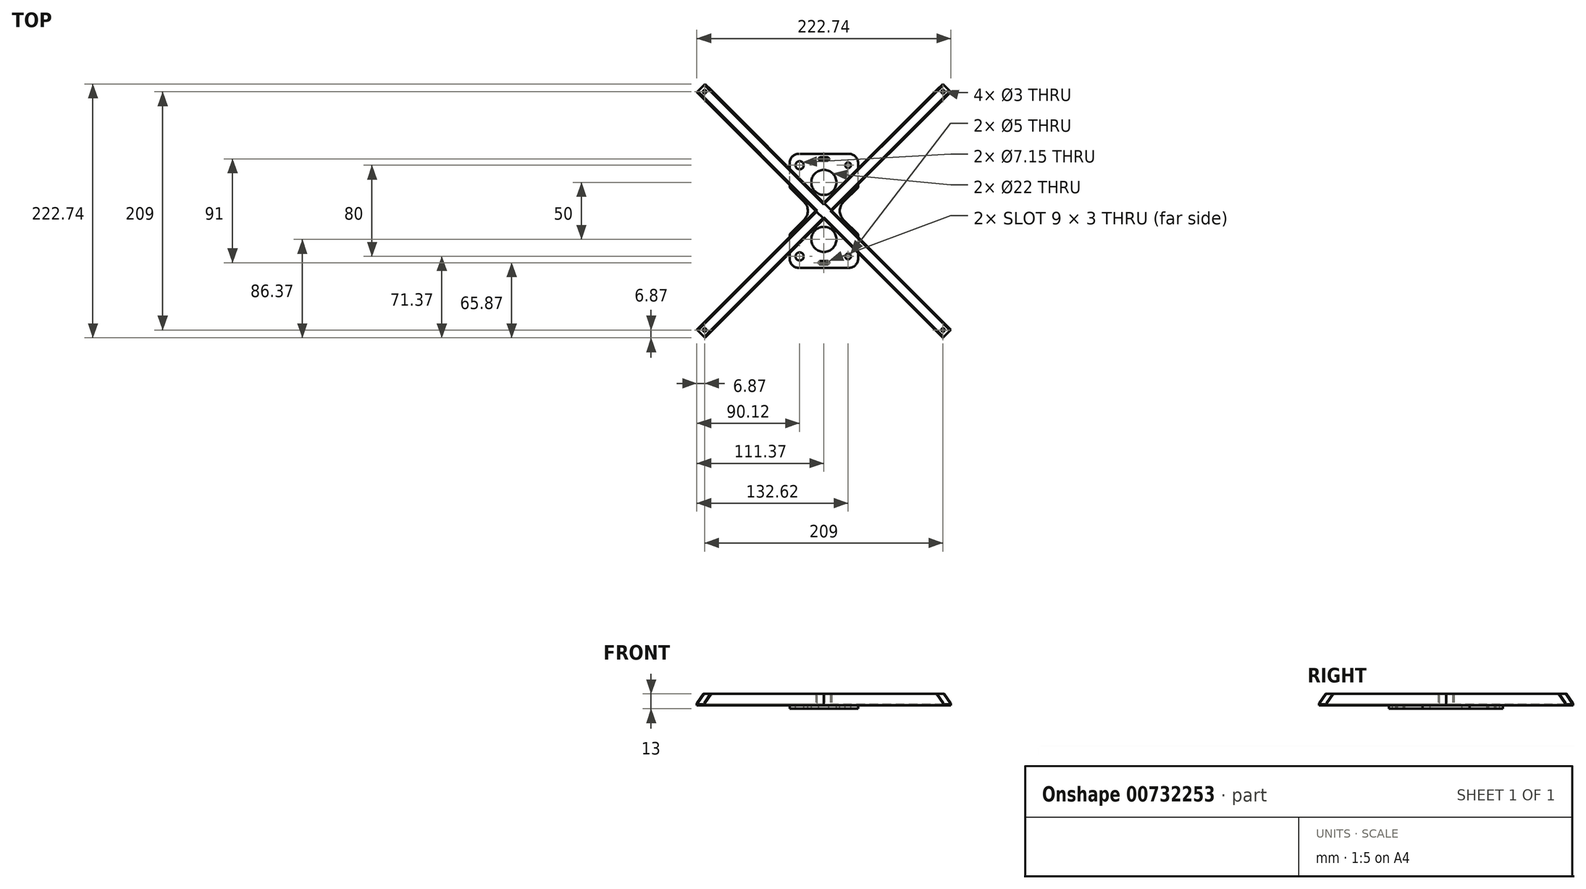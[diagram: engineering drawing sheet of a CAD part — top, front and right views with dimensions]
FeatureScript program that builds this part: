
annotation { "Feature Type Name" : "Feature", "Feature Type Description" : "" }
export const myFeature = defineFeature(function(context is Context, id is Id, definition is map)
    precondition{}
    {
        {
            var Q0;
            Q0=qCreatedBy(makeId("Top.planeOp"),FACE);
            var sketch = newSketch(context, id + "F0", { "sketchPlane" : qUnion([Q0])});
            skLineSegment(sketch, "E0.bottom", {"start": v(30, -50) * mm, "end": v(-30, -50) * mm});
            skLineSegment(sketch, "E0.top", {"start": v(30, 50) * mm, "end": v(-30, 50) * mm});
            skLineSegment(sketch, "E0.left", {"start": v(30, -50) * mm, "end": v(30, 50) * mm});
            skLineSegment(sketch, "E0.right", {"start": v(-30, -50) * mm, "end": v(-30, 50) * mm});
            skPoint(sketch, "E0.middle", {"position": v(0, 0) * mm});
            skSolve(sketch);
        }
        {
            var Q0;
            Q0=qSketchRegion(id+"F0",true);
            extrude(context, id + "F1", {"entities" : qUnion([Q0]), "depth" : 3 * mm, "offsetDistance" : 25 * mm});
        }
        {
            var Q0;
            Q0=makeQuery(id+"F1.opExtrude","CAP_FACE",FACE,{"disambiguationData":[OSD([sQuery(id+"F0.wireOp",EDGE,"E0.bottom"),sQuery(id+"F0.wireOp",EDGE,"E0.top"),sQuery(id+"F0.wireOp",EDGE,"E0.left"),sQuery(id+"F0.wireOp",EDGE,"E0.right")])],"isStart":false});
            var sketch = newSketch(context, id + "F2", { "sketchPlane" : qUnion([Q0])});
            skCircle(sketch, "E1", {"center": v(0, 25) * mm, "radius": 11 * mm});
            skCircle(sketch, "E2", {"center": v(0, -25) * mm, "radius": 11 * mm});
            skCircle(sketch, "E3", {"center": v(25, 0) * mm, "radius": 11 * mm});
            skCircle(sketch, "E4", {"center": v(-25, 0) * mm, "radius": 11 * mm});
            skLineSegment(sketch, "E5", {"start": v(-3, 45.5) * mm, "end": v(3, 45.5) * mm});
            skLineSegment(sketch, "E6", {"start": v(-3, -45.5) * mm, "end": v(3, -45.5) * mm});
            skPoint(sketch, "E7", {"position": v(0, 45.5) * mm});
            skArc(sketch, "E8.0.startCap", {"start": v(-3, 44) * mm, "mid": v(-4.5, 45.5) * mm, "end": v(-3, 47) * mm});
            skArc(sketch, "E8.0.endCap", {"start": v(3, 47) * mm, "mid": v(4.5, 45.5) * mm, "end": v(3, 44) * mm});
            skLineSegment(sketch, "E8.0.left", {"start": v(-3, 47) * mm, "end": v(3, 47) * mm});
            skLineSegment(sketch, "E8.0.right", {"start": v(-3, 44) * mm, "end": v(3, 44) * mm});
            skArc(sketch, "E9.0.startCap", {"start": v(-3, -47) * mm, "mid": v(-4.5, -45.5) * mm, "end": v(-3, -44) * mm});
            skArc(sketch, "E9.0.endCap", {"start": v(3, -44) * mm, "mid": v(4.5, -45.5) * mm, "end": v(3, -47) * mm});
            skLineSegment(sketch, "E9.0.left", {"start": v(-3, -44) * mm, "end": v(3, -44) * mm});
            skLineSegment(sketch, "E9.0.right", {"start": v(-3, -47) * mm, "end": v(3, -47) * mm});
            skSolve(sketch);
        }
        {
            var Q0;
            Q0=makeQuery(id+"F2.imprint","IMPRINT",FACE,{"disambiguationData":[TD([[makeQuery(id+"F2.imprint","IMPRINT",EDGE,{"derivedFrom":sQuery(id+"F2.wireOp",EDGE,"E1")}),-1.0]])]});
            var sketch = newSketch(context, id + "F3", { "sketchPlane" : qUnion([Q0])});
            skLineSegment(sketch, "E10.bottom", {"start": v(21.25, 40) * mm, "end": v(-21.25, 40) * mm, "construction": true});
            skLineSegment(sketch, "E10.top", {"start": v(21.25, -40) * mm, "end": v(-21.25, -40) * mm, "construction": true});
            skLineSegment(sketch, "E10.left", {"start": v(21.25, 40) * mm, "end": v(21.25, -40) * mm, "construction": true});
            skLineSegment(sketch, "E10.right", {"start": v(-21.25, 40) * mm, "end": v(-21.25, -40) * mm, "construction": true});
            skPoint(sketch, "E10.middle", {"position": v(0, 0) * mm});
            skCircle(sketch, "E11", {"center": v(21.25, 40) * mm, "radius": 2.5 * mm});
            skCircle(sketch, "E12", {"center": v(21.25, -40) * mm, "radius": 2.5 * mm});
            skCircle(sketch, "E13", {"center": v(-21.25, -40) * mm, "radius": 3.58 * mm});
            skCircle(sketch, "E14", {"center": v(-21.25, 40) * mm, "radius": 3.57 * mm});
            skSolve(sketch);
        }
        {
            var Q0;
            Q0=qSketchRegion(id+"F3",true);
            extrude(context, id + "F4", {"entities" : qUnion([Q0]), "operationType" : NewBodyOperationType.REMOVE, "endBound" : BoundingType.THROUGH_ALL, "oppositeDirection" : true, "depth" : 25 * mm, "offsetDistance" : 25 * mm});
        }
        {
            var Q0;
            Q0=qSketchRegion(id+"F2",true);
            extrude(context, id + "F5", {"entities" : qUnion([Q0]), "operationType" : NewBodyOperationType.REMOVE, "endBound" : BoundingType.THROUGH_ALL, "oppositeDirection" : true, "depth" : 25 * mm, "offsetDistance" : 25 * mm});
        }
        {
            var Q0;
            Q0=makeQuery(id+"F1.opExtrude","CAP_FACE",FACE,{"disambiguationData":[OSD([sQuery(id+"F0.wireOp",EDGE,"E0.bottom"),sQuery(id+"F0.wireOp",EDGE,"E0.top"),sQuery(id+"F0.wireOp",EDGE,"E0.left"),sQuery(id+"F0.wireOp",EDGE,"E0.right")])],"isStart":false});
            var sketch = newSketch(context, id + "F6", { "sketchPlane" : qUnion([Q0])});
            skLineSegment(sketch, "E15", {"start": v(30, 20.56) * mm, "end": v(30, -20.56) * mm});
            skLineSegment(sketch, "E16", {"start": v(30, -20.56) * mm, "end": v(17.22, -7.78) * mm});
            skLineSegment(sketch, "E17", {"start": v(17.22, -7.78) * mm, "end": v(17.22, 7.78) * mm});
            skLineSegment(sketch, "E18", {"start": v(17.22, 7.78) * mm, "end": v(30, 20.56) * mm});
            skLineSegment(sketch, "E19", {"start": v(-30, 20.56) * mm, "end": v(-17.22, 7.78) * mm});
            skLineSegment(sketch, "E20", {"start": v(-17.22, 7.78) * mm, "end": v(-17.22, -7.78) * mm});
            skLineSegment(sketch, "E21", {"start": v(-17.22, -7.78) * mm, "end": v(-30, -20.56) * mm});
            skLineSegment(sketch, "E22", {"start": v(-30, -20.56) * mm, "end": v(-30, 20.56) * mm});
            skSolve(sketch);
        }
        {
            var Q0;
            Q0=qSketchRegion(id+"F6",true);
            extrude(context, id + "F7", {"entities" : qUnion([Q0]), "operationType" : NewBodyOperationType.REMOVE, "endBound" : BoundingType.THROUGH_ALL, "oppositeDirection" : true, "depth" : 25 * mm, "offsetDistance" : 25 * mm});
        }
        {
            var Q0;
            Q0=makeQuery(id+"F1.opExtrude","SWEPT_EDGE",EDGE,{"disambiguationData":[OSD([sQuery(id+"F0.wireOp",EDGE,"E0.bottom"),sQuery(id+"F0.wireOp",EDGE,"E0.left")])]});
            var Q1;
            Q1=makeQuery(id+"F1.opExtrude","SWEPT_EDGE",EDGE,{"disambiguationData":[OSD([sQuery(id+"F0.wireOp",EDGE,"E0.bottom"),sQuery(id+"F0.wireOp",EDGE,"E0.right")])]});
            var Q2;
            Q2=makeQuery(id+"F1.opExtrude","SWEPT_EDGE",EDGE,{"disambiguationData":[OSD([sQuery(id+"F0.wireOp",EDGE,"E0.top"),sQuery(id+"F0.wireOp",EDGE,"E0.left")])]});
            var Q3;
            Q3=makeQuery(id+"F1.opExtrude","SWEPT_EDGE",EDGE,{"disambiguationData":[OSD([sQuery(id+"F0.wireOp",EDGE,"E0.top"),sQuery(id+"F0.wireOp",EDGE,"E0.right")])]});
            fillet(context, id + "F8", {"entities" : qUnion([Q0, Q1, Q2, Q3]), "radius" : 8 * mm, "tangentPropagation" : true, "allowEdgeOverflow" : false});
        }
        {
            var Q0;
            Q0=makeQuery(id+"F1.opExtrude","CAP_FACE",FACE,{"disambiguationData":[OSD([sQuery(id+"F0.wireOp",EDGE,"E0.bottom"),sQuery(id+"F0.wireOp",EDGE,"E0.top"),sQuery(id+"F0.wireOp",EDGE,"E0.left"),sQuery(id+"F0.wireOp",EDGE,"E0.right")])],"isStart":false});
            var sketch = newSketch(context, id + "F9", { "sketchPlane" : qUnion([Q0])});
            skLineSegment(sketch, "E23", {"start": v(-107.83, 107.83) * mm, "end": v(107.83, -107.83) * mm, "construction": true});
            skLineSegment(sketch, "E24", {"start": v(-104.3, 111.37) * mm, "end": v(-111.37, 104.3) * mm});
            skLineSegment(sketch, "E25", {"start": v(-111.37, 104.3) * mm, "end": v(104.3, -111.37) * mm});
            skLineSegment(sketch, "E26", {"start": v(104.3, -111.37) * mm, "end": v(111.37, -104.3) * mm});
            skLineSegment(sketch, "E27", {"start": v(111.37, -104.3) * mm, "end": v(-104.3, 111.37) * mm});
            skSolve(sketch);
        }
        {
            var Q0;
            Q0=qSketchRegion(id+"F9",true);
            extrude(context, id + "F10", {"entities" : qUnion([Q0]), "depth" : 10 * mm, "offsetDistance" : 25 * mm});
        }
        {
            var Q0;
            Q0=makeQuery(id+"F10.opExtrude","CAP_FACE",FACE,{"disambiguationData":[OSD([sQuery(id+"F9.wireOp",EDGE,"E24"),sQuery(id+"F9.wireOp",EDGE,"E25"),sQuery(id+"F9.wireOp",EDGE,"E26"),sQuery(id+"F9.wireOp",EDGE,"E27")])],"isStart":false});
            var sketch = newSketch(context, id + "F11", { "sketchPlane" : qUnion([Q0])});
            skLineSegment(sketch, "E28", {"start": v(-105, 110.66) * mm, "end": v(-110.66, 105) * mm});
            skLineSegment(sketch, "E29", {"start": v(-110.66, 105) * mm, "end": v(105, -110.66) * mm});
            skLineSegment(sketch, "E30", {"start": v(105, -110.66) * mm, "end": v(110.66, -105) * mm});
            skLineSegment(sketch, "E31", {"start": v(110.66, -105) * mm, "end": v(-105, 110.66) * mm});
            skSolve(sketch);
        }
        {
            var Q0;
            Q0=qSketchRegion(id+"F11",true);
            extrude(context, id + "F12", {"entities" : qUnion([Q0]), "operationType" : NewBodyOperationType.REMOVE, "oppositeDirection" : true, "depth" : 9 * mm, "offsetDistance" : 25 * mm});
        }
        {
            var Q0;
            Q0=makeQuery(id+"F10.opExtrude","SWEPT_FACE",FACE,{"disambiguationData":[OSD([sQuery(id+"F9.wireOp",EDGE,"E27")])]});
            var sketch = newSketch(context, id + "F13", { "sketchPlane" : qUnion([Q0])});
            skLineSegment(sketch, "E32.bottom", {"start": v(5, 13) * mm, "end": v(-5, 13) * mm});
            skLineSegment(sketch, "E32.top", {"start": v(5, 3) * mm, "end": v(-5, 3) * mm});
            skLineSegment(sketch, "E32.left", {"start": v(5, 13) * mm, "end": v(5, 3) * mm});
            skLineSegment(sketch, "E32.right", {"start": v(-5, 13) * mm, "end": v(-5, 3) * mm});
            skSolve(sketch);
        }
        {
            var Q0;
            Q0=qSketchRegion(id+"F13",true);
            extrude(context, id + "F14", {"entities" : qUnion([Q0]), "depth" : (305 / 2 - 5) * mm, "offsetDistance" : 25 * mm});
        }
        {
            var Q0;
            Q0=makeQuery(id+"F14.opExtrude","CAP_FACE",FACE,{"disambiguationData":[OSD([sQuery(id+"F13.wireOp",EDGE,"E32.bottom"),sQuery(id+"F13.wireOp",EDGE,"E32.top"),sQuery(id+"F13.wireOp",EDGE,"E32.left"),sQuery(id+"F13.wireOp",EDGE,"E32.right")])],"isStart":false});
            var sketch = newSketch(context, id + "F15", { "sketchPlane" : qUnion([Q0])});
            skLineSegment(sketch, "E33.bottom", {"start": v(4, 13) * mm, "end": v(-4, 13) * mm});
            skLineSegment(sketch, "E33.top", {"start": v(4, 4) * mm, "end": v(-4, 4) * mm});
            skLineSegment(sketch, "E33.left", {"start": v(4, 13) * mm, "end": v(4, 4) * mm});
            skLineSegment(sketch, "E33.right", {"start": v(-4, 13) * mm, "end": v(-4, 4) * mm});
            skSolve(sketch);
        }
        {
            var Q0;
            Q0=qSketchRegion(id+"F15",true);
            extrude(context, id + "F16", {"entities" : qUnion([Q0]), "operationType" : NewBodyOperationType.REMOVE, "endBound" : BoundingType.THROUGH_ALL, "oppositeDirection" : true, "depth" : 25 * mm, "offsetDistance" : 25 * mm});
        }
        {
            var Q0;
            Q0=qCreatedBy(makeId("Front.planeOp"),FACE);
            var Q1;
            Q1=qCreatedBy(makeId("Right.planeOp"),FACE);
            cPlane(context, id + "F17", {"entities" : qUnion([Q0, Q1]), "cplaneType" : CPlaneType.MID_PLANE, "offset" : 25 * mm, "width" : 150 * mm, "height" : 150 * mm});
        }
        {
            var Q0;
            Q0=makeQuery(id+"F14.opExtrude","SWEPT_BODY",BODY,{"disambiguationData":[OSD([sQuery(id+"F13.wireOp",EDGE,"E32.bottom"),sQuery(id+"F13.wireOp",EDGE,"E32.top"),sQuery(id+"F13.wireOp",EDGE,"E32.left"),sQuery(id+"F13.wireOp",EDGE,"E32.right")])]});
            var Q1;
            Q1=qCreatedBy(id+"F17.planeOp",FACE);
            mirror(context, id + "F18", {"entities" : qUnion([Q0]), "mirrorPlane" : qUnion([Q1])});
        }
        {
            var Q0;
            {var subQ0=sQuery(id+"F13.wireOp",EDGE,"E32.bottom");var subQ1=sQuery(id+"F13.wireOp",EDGE,"E32.left");Q0=makeQuery(id+"F16.boolean.opBoolean","SPLIT",EDGE,{"disambiguationData":[TD([makeQuery(id+"F14.opExtrude","SWEPT_FACE",FACE,{"disambiguationData":[OSD([subQ1])]})])],"derivedFrom":makeQuery(id+"F14.opExtrude","CAP_EDGE",EDGE,{"disambiguationData":[OSD([subQ0])],"isStart":false})});}
            var Q1;
            {var subQ0=sQuery(id+"F13.wireOp",EDGE,"E32.bottom");var subQ1=sQuery(id+"F13.wireOp",EDGE,"E32.right");Q1=makeQuery(id+"F16.boolean.opBoolean","SPLIT",EDGE,{"disambiguationData":[TD([makeQuery(id+"F14.opExtrude","SWEPT_FACE",FACE,{"disambiguationData":[OSD([subQ1])]})])],"derivedFrom":makeQuery(id+"F14.opExtrude","CAP_EDGE",EDGE,{"disambiguationData":[OSD([subQ0])],"isStart":false})});}
            var Q2;
            {var subQ0=sQuery(id+"F9.wireOp",EDGE,"E26");var subQ1=sQuery(id+"F9.wireOp",EDGE,"E25");Q2=makeQuery(id+"F12.boolean.opBoolean","SPLIT",EDGE,{"disambiguationData":[TD([makeQuery(id+"F10.opExtrude","SWEPT_FACE",FACE,{"disambiguationData":[OSD([subQ1])]})])],"derivedFrom":makeQuery(id+"F10.opExtrude","CAP_EDGE",EDGE,{"disambiguationData":[OSD([subQ0])],"isStart":false})});}
            var Q3;
            {var subQ0=sQuery(id+"F9.wireOp",EDGE,"E27");var subQ1=sQuery(id+"F9.wireOp",EDGE,"E26");Q3=makeQuery(id+"F12.boolean.opBoolean","SPLIT",EDGE,{"disambiguationData":[TD([makeQuery(id+"F10.opExtrude","SWEPT_FACE",FACE,{"disambiguationData":[OSD([subQ0])]})])],"derivedFrom":makeQuery(id+"F10.opExtrude","CAP_EDGE",EDGE,{"disambiguationData":[OSD([subQ1])],"isStart":false})});}
            var Q4;
            {var subQ0=sQuery(id+"F13.wireOp",EDGE,"E32.bottom");var subQ1=sQuery(id+"F13.wireOp",EDGE,"E32.right");Q4=makeQuery(id+"F18.opPattern","COPY",EDGE,{"derivedFrom":makeQuery(id+"F16.boolean.opBoolean","SPLIT",EDGE,{"disambiguationData":[TD([makeQuery(id+"F14.opExtrude","SWEPT_FACE",FACE,{"disambiguationData":[OSD([subQ1])]})])],"derivedFrom":makeQuery(id+"F14.opExtrude","CAP_EDGE",EDGE,{"disambiguationData":[OSD([subQ0])],"isStart":false})}),"instanceName":"1"});}
            var Q5;
            {var subQ0=sQuery(id+"F13.wireOp",EDGE,"E32.bottom");var subQ1=sQuery(id+"F13.wireOp",EDGE,"E32.left");Q5=makeQuery(id+"F18.opPattern","COPY",EDGE,{"derivedFrom":makeQuery(id+"F16.boolean.opBoolean","SPLIT",EDGE,{"disambiguationData":[TD([makeQuery(id+"F14.opExtrude","SWEPT_FACE",FACE,{"disambiguationData":[OSD([subQ1])]})])],"derivedFrom":makeQuery(id+"F14.opExtrude","CAP_EDGE",EDGE,{"disambiguationData":[OSD([subQ0])],"isStart":false})}),"instanceName":"1"});}
            var Q6;
            {var subQ0=sQuery(id+"F9.wireOp",EDGE,"E24");var subQ1=sQuery(id+"F9.wireOp",EDGE,"E27");Q6=makeQuery(id+"F12.boolean.opBoolean","SPLIT",EDGE,{"disambiguationData":[TD([makeQuery(id+"F10.opExtrude","SWEPT_FACE",FACE,{"disambiguationData":[OSD([subQ1])]})])],"derivedFrom":makeQuery(id+"F10.opExtrude","CAP_EDGE",EDGE,{"disambiguationData":[OSD([subQ0])],"isStart":false})});}
            var Q7;
            {var subQ0=sQuery(id+"F9.wireOp",EDGE,"E24");var subQ1=sQuery(id+"F9.wireOp",EDGE,"E25");Q7=makeQuery(id+"F12.boolean.opBoolean","SPLIT",EDGE,{"disambiguationData":[TD([makeQuery(id+"F10.opExtrude","SWEPT_FACE",FACE,{"disambiguationData":[OSD([subQ1])]})])],"derivedFrom":makeQuery(id+"F10.opExtrude","CAP_EDGE",EDGE,{"disambiguationData":[OSD([subQ0])],"isStart":false})});}
            chamfer(context, id + "F19", {"entities" : qUnion([Q0, Q1, Q2, Q3, Q4, Q5, Q6, Q7]), "width" : 8 * mm, "tangentPropagation" : true});
        }
        {
            var Q0;
            Q0=makeQuery(id+"F12.boolean.opBoolean","COPY",FACE,{"derivedFrom":makeQuery(id+"F12.opExtrude","CAP_FACE",FACE,{"disambiguationData":[OSD([sQuery(id+"F11.wireOp",EDGE,"E28"),sQuery(id+"F11.wireOp",EDGE,"E29"),sQuery(id+"F11.wireOp",EDGE,"E30"),sQuery(id+"F11.wireOp",EDGE,"E31")])],"isStart":false})});
            var sketch = newSketch(context, id + "F20", { "sketchPlane" : qUnion([Q0])});
            skLineSegment(sketch, "E34.bottom", {"start": v(-104.5, -104.5) * mm, "end": v(104.5, -104.5) * mm, "construction": true});
            skLineSegment(sketch, "E34.top", {"start": v(-104.5, 104.5) * mm, "end": v(104.5, 104.5) * mm, "construction": true});
            skLineSegment(sketch, "E34.left", {"start": v(-104.5, -104.5) * mm, "end": v(-104.5, 104.5) * mm, "construction": true});
            skLineSegment(sketch, "E34.right", {"start": v(104.5, -104.5) * mm, "end": v(104.5, 104.5) * mm, "construction": true});
            skPoint(sketch, "E34.middle", {"position": v(0, 0) * mm});
            skCircle(sketch, "E35", {"center": v(-104.5, -104.5) * mm, "radius": 1.5 * mm});
            skCircle(sketch, "E36", {"center": v(104.5, -104.5) * mm, "radius": 1.5 * mm});
            skCircle(sketch, "E37", {"center": v(104.5, 104.5) * mm, "radius": 1.5 * mm});
            skCircle(sketch, "E38", {"center": v(-104.5, 104.5) * mm, "radius": 1.5 * mm});
            skSolve(sketch);
        }
        {
            var Q0;
            Q0=qSketchRegion(id+"F20",true);
            extrude(context, id + "F21", {"entities" : qUnion([Q0]), "operationType" : NewBodyOperationType.REMOVE, "endBound" : BoundingType.THROUGH_ALL, "oppositeDirection" : true, "depth" : 25 * mm, "offsetDistance" : 25 * mm});
        }
    });
